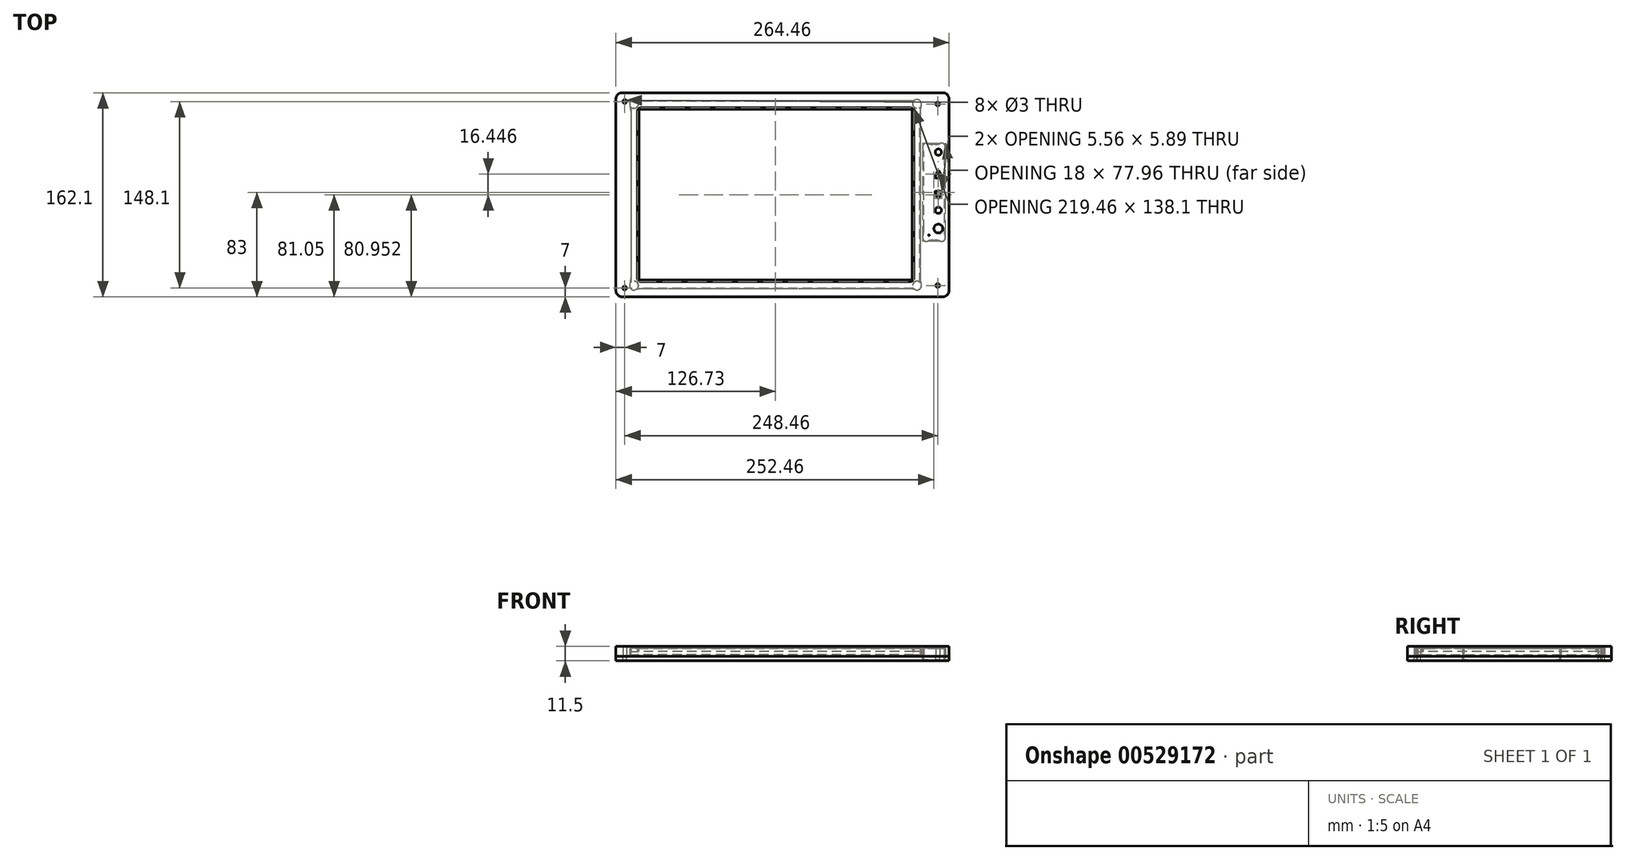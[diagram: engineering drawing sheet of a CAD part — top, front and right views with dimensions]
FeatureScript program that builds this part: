
annotation { "Feature Type Name" : "Feature", "Feature Type Description" : "" }
export const myFeature = defineFeature(function(context is Context, id is Id, definition is map)
    precondition{}
    {
        {
            var Q0;
            Q0=qCreatedBy(makeId("Top.planeOp"),FACE);
            var sketch = newSketch(context, id + "F0", { "sketchPlane" : qUnion([Q0])});
            skLineSegment(sketch, "E0.bottom", {"start": v(-121.73, 81.05) * mm, "end": v(132.73, 81.05) * mm});
            skLineSegment(sketch, "E0.top", {"start": v(-121.73, -81.05) * mm, "end": v(132.73, -81.05) * mm});
            skLineSegment(sketch, "E0.left", {"start": v(-126.73, 76.05) * mm, "end": v(-126.73, -76.05) * mm});
            skLineSegment(sketch, "E0.right", {"start": v(137.73, 76.05) * mm, "end": v(137.73, -76.05) * mm});
            skLineSegment(sketch, "E1.bottom", {"start": v(-106.73, 69.05) * mm, "end": v(106.73, 69.05) * mm});
            skLineSegment(sketch, "E1.top", {"start": v(-106.73, -69.05) * mm, "end": v(106.73, -69.05) * mm});
            skLineSegment(sketch, "E1.left", {"start": v(-109.73, 66.05) * mm, "end": v(-109.73, -66.05) * mm});
            skLineSegment(sketch, "E1.right", {"start": v(109.73, 66.05) * mm, "end": v(109.73, -66.05) * mm});
            skPoint(sketch, "E2.visualSharp", {"position": v(-126.73, 81.05) * mm});
            skArc(sketch, "E2.filletArc", {"start": v(-121.73, 81.05) * mm, "mid": v(-125.27, 79.59) * mm, "end": v(-126.73, 76.05) * mm});
            skPoint(sketch, "E3.visualSharp", {"position": v(-126.73, -81.05) * mm});
            skArc(sketch, "E3.filletArc", {"start": v(-126.73, -76.05) * mm, "mid": v(-125.27, -79.59) * mm, "end": v(-121.73, -81.05) * mm});
            skPoint(sketch, "E4.visualSharp", {"position": v(137.73, -81.05) * mm});
            skArc(sketch, "E4.filletArc", {"start": v(132.73, -81.05) * mm, "mid": v(136.27, -79.59) * mm, "end": v(137.73, -76.05) * mm});
            skPoint(sketch, "E5.visualSharp", {"position": v(137.73, 81.05) * mm});
            skArc(sketch, "E5.filletArc", {"start": v(137.73, 76.05) * mm, "mid": v(136.27, 79.59) * mm, "end": v(132.73, 81.05) * mm});
            skCircle(sketch, "E6", {"center": v(129.23, 33.85) * mm, "radius": 2.5 * mm});
            skLineSegment(sketch, "E7", {"start": v(129.23, 33.85) * mm, "end": v(129.23, -36.05) * mm, "construction": true});
            skCircle(sketch, "E8", {"center": v(129.23, -12.32) * mm, "radius": 2.5 * mm});
            skPoint(sketch, "E9", {"position": v(129.23, -1.1) * mm});
            skCircle(sketch, "E10", {"center": v(129.23, -26.87) * mm, "radius": 3.5 * mm});
            skCircle(sketch, "E11", {"center": v(129.23, 15.98) * mm, "radius": 4 * mm, "construction": true});
            skLineSegment(sketch, "E12", {"start": v(128.78, 19) * mm, "end": v(126.5, 14.12) * mm});
            skLineSegment(sketch, "E13", {"start": v(126.95, 13.4) * mm, "end": v(131.5, 13.4) * mm});
            skLineSegment(sketch, "E14", {"start": v(131.96, 14.12) * mm, "end": v(129.68, 19) * mm});
            skCircle(sketch, "E15", {"center": v(129.23, 0.28) * mm, "radius": 4 * mm, "construction": true});
            skLineSegment(sketch, "E16", {"start": v(129.68, -2.75) * mm, "end": v(131.96, 2.13) * mm});
            skLineSegment(sketch, "E17", {"start": v(131.5, 2.85) * mm, "end": v(126.95, 2.85) * mm});
            skLineSegment(sketch, "E18", {"start": v(126.5, 2.13) * mm, "end": v(128.78, -2.75) * mm});
            skLineSegment(sketch, "E19.bottom", {"start": v(117.73, 39.95) * mm, "end": v(133.73, 39.95) * mm, "construction": true});
            skLineSegment(sketch, "E19.top", {"start": v(117.73, -36.05) * mm, "end": v(133.73, -36.05) * mm, "construction": true});
            skLineSegment(sketch, "E19.left", {"start": v(117.73, 39.95) * mm, "end": v(117.73, -36.05) * mm, "construction": true});
            skLineSegment(sketch, "E19.right", {"start": v(133.73, 39.95) * mm, "end": v(133.73, -36.05) * mm, "construction": true});
            skPoint(sketch, "E20.visualSharp", {"position": v(129.23, 19.98) * mm});
            skArc(sketch, "E20.filletArc", {"start": v(129.68, 19) * mm, "mid": v(129.23, 19.3) * mm, "end": v(128.78, 19) * mm});
            skPoint(sketch, "E21.visualSharp", {"position": v(126.17, 13.4) * mm});
            skArc(sketch, "E21.filletArc", {"start": v(126.5, 14.12) * mm, "mid": v(126.53, 13.64) * mm, "end": v(126.95, 13.4) * mm});
            skPoint(sketch, "E22.visualSharp", {"position": v(132.3, 13.4) * mm});
            skArc(sketch, "E22.filletArc", {"start": v(131.5, 13.4) * mm, "mid": v(131.93, 13.64) * mm, "end": v(131.96, 14.12) * mm});
            skPoint(sketch, "E23.visualSharp", {"position": v(126.17, 2.85) * mm});
            skArc(sketch, "E23.filletArc", {"start": v(126.95, 2.85) * mm, "mid": v(126.53, 2.61) * mm, "end": v(126.5, 2.13) * mm});
            skPoint(sketch, "E24.visualSharp", {"position": v(132.3, 2.85) * mm});
            skArc(sketch, "E24.filletArc", {"start": v(131.96, 2.13) * mm, "mid": v(131.93, 2.61) * mm, "end": v(131.5, 2.85) * mm});
            skPoint(sketch, "E25.visualSharp", {"position": v(129.23, -3.72) * mm});
            skArc(sketch, "E25.filletArc", {"start": v(128.78, -2.75) * mm, "mid": v(129.23, -3.04) * mm, "end": v(129.68, -2.75) * mm});
            skCircle(sketch, "E26", {"center": v(121.73, -32.05) * mm, "radius": 0.35 * mm});
            skCircle(sketch, "E27", {"center": v(128.73, 72.05) * mm, "radius": 1.5 * mm});
            skCircle(sketch, "E28", {"center": v(-119.73, 74.05) * mm, "radius": 1.5 * mm});
            skCircle(sketch, "E29.MirrorC", {"center": v(128.73, -72.05) * mm, "radius": 1.5 * mm});
            skCircle(sketch, "E30.MirrorC", {"center": v(-119.73, -74.05) * mm, "radius": 1.5 * mm});
            skPoint(sketch, "E31.visualSharp", {"position": v(-109.73, 69.05) * mm});
            skArc(sketch, "E31.filletArc", {"start": v(-106.73, 69.05) * mm, "mid": v(-108.85, 68.17) * mm, "end": v(-109.73, 66.05) * mm});
            skPoint(sketch, "E32.visualSharp", {"position": v(-109.73, -69.05) * mm});
            skArc(sketch, "E32.filletArc", {"start": v(-109.73, -66.05) * mm, "mid": v(-108.85, -68.17) * mm, "end": v(-106.73, -69.05) * mm});
            skPoint(sketch, "E33.visualSharp", {"position": v(109.73, -69.05) * mm});
            skArc(sketch, "E33.filletArc", {"start": v(106.73, -69.05) * mm, "mid": v(108.85, -68.17) * mm, "end": v(109.73, -66.05) * mm});
            skPoint(sketch, "E34.visualSharp", {"position": v(109.73, 69.05) * mm});
            skArc(sketch, "E34.filletArc", {"start": v(109.73, 66.05) * mm, "mid": v(108.85, 68.17) * mm, "end": v(106.73, 69.05) * mm});
            skSolve(sketch);
        }
        {
            var Q0;
            Q0=makeQuery(id+"F0.imprint","IMPRINT",FACE,{"disambiguationData":[TD([[makeQuery(id+"F0.imprint","IMPRINT",EDGE,{"derivedFrom":sQuery(id+"F0.wireOp",EDGE,"E0.bottom")}),-1.0]])]});
            extrude(context, id + "F1", {"entities" : qUnion([Q0]), "depth" : 8 * mm, "offsetDistance" : 25 * mm});
        }
        {
            var Q0;
            Q0=makeQuery(id+"F1.opExtrude","CAP_FACE",FACE,{"disambiguationData":[OSD([sQuery(id+"F0.wireOp",EDGE,"E0.bottom"),sQuery(id+"F0.wireOp",EDGE,"E0.top"),sQuery(id+"F0.wireOp",EDGE,"E0.left"),sQuery(id+"F0.wireOp",EDGE,"E0.right"),sQuery(id+"F0.wireOp",EDGE,"E1.bottom"),sQuery(id+"F0.wireOp",EDGE,"E1.top"),sQuery(id+"F0.wireOp",EDGE,"E1.left"),sQuery(id+"F0.wireOp",EDGE,"E1.right"),sQuery(id+"F0.wireOp",EDGE,"E2.filletArc"),sQuery(id+"F0.wireOp",EDGE,"E3.filletArc"),sQuery(id+"F0.wireOp",EDGE,"E4.filletArc"),sQuery(id+"F0.wireOp",EDGE,"E5.filletArc"),sQuery(id+"F0.wireOp",EDGE,"E6"),sQuery(id+"F0.wireOp",EDGE,"E8"),sQuery(id+"F0.wireOp",EDGE,"E10"),sQuery(id+"F0.wireOp",EDGE,"E12"),sQuery(id+"F0.wireOp",EDGE,"E13"),sQuery(id+"F0.wireOp",EDGE,"E14"),sQuery(id+"F0.wireOp",EDGE,"E16"),sQuery(id+"F0.wireOp",EDGE,"E17"),sQuery(id+"F0.wireOp",EDGE,"E18"),sQuery(id+"F0.wireOp",EDGE,"E20.filletArc"),sQuery(id+"F0.wireOp",EDGE,"E21.filletArc"),sQuery(id+"F0.wireOp",EDGE,"E22.filletArc"),sQuery(id+"F0.wireOp",EDGE,"E23.filletArc"),sQuery(id+"F0.wireOp",EDGE,"E24.filletArc"),sQuery(id+"F0.wireOp",EDGE,"E25.filletArc"),sQuery(id+"F0.wireOp",EDGE,"E26"),sQuery(id+"F0.wireOp",EDGE,"E27"),sQuery(id+"F0.wireOp",EDGE,"E28"),sQuery(id+"F0.wireOp",EDGE,"E29.MirrorC"),sQuery(id+"F0.wireOp",EDGE,"E30.MirrorC")])],"isStart":true});
            var sketch = newSketch(context, id + "F2", { "sketchPlane" : qUnion([Q0])});
            skLineSegment(sketch, "E35.bottom", {"start": v(114.8, -74.6) * mm, "end": v(-114.8, -74.6) * mm});
            skLineSegment(sketch, "E35.top", {"start": v(114.8, 74.6) * mm, "end": v(-114.8, 74.6) * mm});
            skLineSegment(sketch, "E35.left", {"start": v(114.8, -74.6) * mm, "end": v(114.8, 74.6) * mm});
            skLineSegment(sketch, "E35.right", {"start": v(-114.8, -74.6) * mm, "end": v(-114.8, 74.6) * mm});
            skSolve(sketch);
        }
        {
            var Q0;
            Q0 = qSketchRegion(id + "F2", true);
            extrude(context, id + "F3", {"entities" : qUnion([Q0]), "operationType" : NewBodyOperationType.REMOVE, "oppositeDirection" : true, "depth" : 6.5 * mm, "offsetDistance" : 25 * mm});
        }
        {
            var Q0;
            Q0 = qSketchRegion(id + "F2", true);
            extrude(context, id + "F4", {"entities" : qUnion([Q0]), "oppositeDirection" : true, "depth" : 6.5 * mm, "offsetDistance" : 25 * mm, "hasSecondDirection" : true, "secondDirectionOppositeDirection" : true, "secondDirectionDepth" : 4 * mm});
        }
        {
            var Q0;
            Q0=makeQuery(id+"F4.opExtrude","CAP_FACE",FACE,{"disambiguationData":[OSD([sQuery(id+"F2.wireOp",EDGE,"E35.bottom"),sQuery(id+"F2.wireOp",EDGE,"E35.top"),sQuery(id+"F2.wireOp",EDGE,"E35.left"),sQuery(id+"F2.wireOp",EDGE,"E35.right")])],"isStart":false});
            var sketch = newSketch(context, id + "F5", { "sketchPlane" : qUnion([Q0])});
            skLineSegment(sketch, "E36.bottom", {"start": v(-108.48, 67.8) * mm, "end": v(108.48, 67.8) * mm});
            skLineSegment(sketch, "E36.top", {"start": v(-108.48, -67.8) * mm, "end": v(108.48, -67.8) * mm});
            skLineSegment(sketch, "E36.left", {"start": v(-108.48, 67.8) * mm, "end": v(-108.48, -67.8) * mm});
            skLineSegment(sketch, "E36.right", {"start": v(108.48, 67.8) * mm, "end": v(108.48, -67.8) * mm});
            skSolve(sketch);
        }
        {
            var Q0;
            Q0 = qSketchRegion(id + "F5", true);
            extrude(context, id + "F6", {"entities" : qUnion([Q0]), "operationType" : NewBodyOperationType.ADD, "depth" : 0.5 * mm, "offsetDistance" : 25 * mm});
        }
        {
            var Q0;
            Q0=makeQuery(id+"F0.imprint","IMPRINT",FACE,{"disambiguationData":[TD([[makeQuery(id+"F0.imprint","IMPRINT",EDGE,{"derivedFrom":sQuery(id+"F0.wireOp",EDGE,"E0.bottom")}),-1.0]])]});
            var sketch = newSketch(context, id + "F7", { "sketchPlane" : qUnion([Q0])});
            skLineSegment(sketch, "E37.bottom", {"start": v(131.73, 40.95) * mm, "end": v(119.73, 40.95) * mm, "construction": true});
            skLineSegment(sketch, "E37.top", {"start": v(131.73, -37.05) * mm, "end": v(119.73, -37.05) * mm, "construction": true});
            skLineSegment(sketch, "E37.left", {"start": v(134.73, 37.95) * mm, "end": v(134.73, -34.05) * mm, "construction": true});
            skLineSegment(sketch, "E37.right", {"start": v(116.73, 37.95) * mm, "end": v(116.73, -34.05) * mm, "construction": true});
            skPoint(sketch, "E38.visualSharp", {"position": v(134.73, 40.95) * mm});
            skArc(sketch, "E38.filletArc", {"start": v(134.73, 37.95) * mm, "mid": v(133.85, 40.07) * mm, "end": v(131.73, 40.95) * mm});
            skPoint(sketch, "E39.visualSharp", {"position": v(116.73, 40.95) * mm});
            skArc(sketch, "E39.filletArc", {"start": v(119.73, 40.95) * mm, "mid": v(117.6, 40.07) * mm, "end": v(116.73, 37.95) * mm});
            skPoint(sketch, "E40.visualSharp", {"position": v(116.73, -37.05) * mm});
            skArc(sketch, "E40.filletArc", {"start": v(116.73, -34.05) * mm, "mid": v(117.6, -36.17) * mm, "end": v(119.73, -37.05) * mm});
            skPoint(sketch, "E41.visualSharp", {"position": v(134.73, -37.05) * mm});
            skArc(sketch, "E41.filletArc", {"start": v(131.73, -37.05) * mm, "mid": v(133.85, -36.17) * mm, "end": v(134.73, -34.05) * mm});
            skArc(sketch, "E42", {"start": v(119.73, -37.05) * mm, "mid": v(120.32, -37) * mm, "end": v(120.88, -36.82) * mm});
            skArc(sketch, "E43", {"start": v(130.58, -36.82) * mm, "mid": v(131.14, -37) * mm, "end": v(131.73, -37.05) * mm});
            skLineSegment(sketch, "E44", {"start": v(124.73, -36.05) * mm, "end": v(126.73, -36.05) * mm});
            skArc(sketch, "E45", {"start": v(116.73, -34.05) * mm, "mid": v(116.76, -33.6) * mm, "end": v(116.86, -33.18) * mm});
            skArc(sketch, "E46", {"start": v(116.73, 37.95) * mm, "mid": v(116.76, 37.5) * mm, "end": v(116.86, 37.08) * mm});
            skLineSegment(sketch, "E47", {"start": v(117.73, -27.34) * mm, "end": v(117.73, 31.24) * mm});
            skPoint(sketch, "E48.orphan", {"position": v(119.73, 34.95) * mm});
            skArc(sketch, "E49", {"start": v(119.73, 40.95) * mm, "mid": v(120.32, 40.9) * mm, "end": v(120.88, 40.72) * mm});
            skArc(sketch, "E50", {"start": v(131.73, 40.95) * mm, "mid": v(131.14, 40.9) * mm, "end": v(130.58, 40.72) * mm});
            skLineSegment(sketch, "E51", {"start": v(126.73, 39.95) * mm, "end": v(124.73, 39.95) * mm});
            skArc(sketch, "E52", {"start": v(134.73, 37.95) * mm, "mid": v(134.7, 37.5) * mm, "end": v(134.6, 37.08) * mm});
            skArc(sketch, "E53", {"start": v(134.73, -34.05) * mm, "mid": v(134.7, -33.6) * mm, "end": v(134.6, -33.18) * mm});
            skLineSegment(sketch, "E54", {"start": v(133.73, 31.24) * mm, "end": v(133.73, -27.34) * mm});
            skPoint(sketch, "E55.visualSharp", {"position": v(133.73, 35.71) * mm});
            skArc(sketch, "E55.filletArc", {"start": v(134.6, 37.08) * mm, "mid": v(133.95, 34.2) * mm, "end": v(133.73, 31.24) * mm});
            skPoint(sketch, "E56.visualSharp", {"position": v(133.73, -31.81) * mm});
            skArc(sketch, "E56.filletArc", {"start": v(133.73, -27.34) * mm, "mid": v(133.95, -30.3) * mm, "end": v(134.6, -33.18) * mm});
            skPoint(sketch, "E57.visualSharp", {"position": v(117.73, -31.81) * mm});
            skArc(sketch, "E57.filletArc", {"start": v(116.86, -33.18) * mm, "mid": v(117.51, -30.3) * mm, "end": v(117.73, -27.34) * mm});
            skPoint(sketch, "E58.visualSharp", {"position": v(117.73, 35.71) * mm});
            skArc(sketch, "E58.filletArc", {"start": v(117.73, 31.24) * mm, "mid": v(117.51, 34.2) * mm, "end": v(116.86, 37.08) * mm});
            skPoint(sketch, "E59.visualSharp", {"position": v(121.97, 39.95) * mm});
            skArc(sketch, "E59.filletArc", {"start": v(120.88, 40.72) * mm, "mid": v(122.77, 40.14) * mm, "end": v(124.73, 39.95) * mm});
            skPoint(sketch, "E60.visualSharp", {"position": v(129.5, 39.95) * mm});
            skArc(sketch, "E60.filletArc", {"start": v(126.73, 39.95) * mm, "mid": v(128.7, 40.14) * mm, "end": v(130.58, 40.72) * mm});
            skPoint(sketch, "E61.visualSharp", {"position": v(121.97, -36.05) * mm});
            skArc(sketch, "E61.filletArc", {"start": v(124.73, -36.05) * mm, "mid": v(122.77, -36.24) * mm, "end": v(120.88, -36.82) * mm});
            skPoint(sketch, "E62.visualSharp", {"position": v(129.5, -36.05) * mm});
            skArc(sketch, "E62.filletArc", {"start": v(130.58, -36.82) * mm, "mid": v(128.7, -36.24) * mm, "end": v(126.73, -36.05) * mm});
            skSolve(sketch);
        }
        {
            var Q0;
            Q0 = qSketchRegion(id + "F7", true);
            extrude(context, id + "F8", {"entities" : qUnion([Q0]), "operationType" : NewBodyOperationType.REMOVE, "depth" : 6.5 * mm, "offsetDistance" : 25 * mm});
        }
        {
            var Q0;
            Q0=qCreatedBy(makeId("Top.planeOp"),FACE);
            var sketch = newSketch(context, id + "F9", { "sketchPlane" : qUnion([Q0])});
            skLineSegment(sketch, "E63.0", {"start": v(132.73, -81.05) * mm, "end": v(-121.73, -81.05) * mm});
            skArc(sketch, "E63.1", {"start": v(137.73, -76.05) * mm, "mid": v(136.27, -79.59) * mm, "end": v(132.73, -81.05) * mm});
            skArc(sketch, "E63.2", {"start": v(-121.73, -81.05) * mm, "mid": v(-125.27, -79.59) * mm, "end": v(-126.73, -76.05) * mm});
            skLineSegment(sketch, "E63.3", {"start": v(137.73, 76.05) * mm, "end": v(137.73, -76.05) * mm});
            skLineSegment(sketch, "E63.4", {"start": v(-126.73, -76.05) * mm, "end": v(-126.73, 76.05) * mm});
            skArc(sketch, "E63.5", {"start": v(-126.73, 76.05) * mm, "mid": v(-125.27, 79.59) * mm, "end": v(-121.73, 81.05) * mm});
            skLineSegment(sketch, "E63.6", {"start": v(-121.73, 81.05) * mm, "end": v(132.73, 81.05) * mm});
            skArc(sketch, "E63.7", {"start": v(132.73, 81.05) * mm, "mid": v(136.27, 79.59) * mm, "end": v(137.73, 76.05) * mm});
            skCircle(sketch, "E64.0", {"center": v(128.73, 72.05) * mm, "radius": 1.5 * mm});
            skCircle(sketch, "E65.0", {"center": v(128.73, -72.05) * mm, "radius": 1.5 * mm});
            skCircle(sketch, "E66.0", {"center": v(-119.73, -74.05) * mm, "radius": 1.5 * mm});
            skCircle(sketch, "E67.0", {"center": v(-119.73, 74.05) * mm, "radius": 1.5 * mm});
            skSolve(sketch);
        }
        {
            var Q0;
            Q0 = qSketchRegion(id + "F9", true);
            extrude(context, id + "F10", {"entities" : qUnion([Q0]), "oppositeDirection" : true, "depth" : 3.5 * mm, "offsetDistance" : 25 * mm});
        }
        {
            var Q0;
            Q0 = qSketchRegion(id + "F7", true);
            extrude(context, id + "F11", {"entities" : qUnion([Q0]), "operationType" : NewBodyOperationType.REMOVE, "oppositeDirection" : true, "depth" : 2.7 * mm, "offsetDistance" : 25 * mm});
        }
        {
            var Q0;
            Q0=makeQuery(id+"F10.opExtrude","CAP_FACE",FACE,{"disambiguationData":[OSD([sQuery(id+"F9.wireOp",EDGE,"E63.0"),sQuery(id+"F9.wireOp",EDGE,"E63.1"),sQuery(id+"F9.wireOp",EDGE,"E63.2"),sQuery(id+"F9.wireOp",EDGE,"E63.3"),sQuery(id+"F9.wireOp",EDGE,"E63.4"),sQuery(id+"F9.wireOp",EDGE,"E63.5"),sQuery(id+"F9.wireOp",EDGE,"E63.6"),sQuery(id+"F9.wireOp",EDGE,"E63.7")])],"isStart":true});
            var sketch = newSketch(context, id + "F12", { "sketchPlane" : qUnion([Q0])});
            skLineSegment(sketch, "E68.bottom", {"start": v(113.58, -74.25) * mm, "end": v(-113.58, -74.25) * mm});
            skLineSegment(sketch, "E68.top", {"start": v(113.58, 74.25) * mm, "end": v(-113.58, 74.25) * mm});
            skLineSegment(sketch, "E68.left", {"start": v(114.58, -73.25) * mm, "end": v(114.58, 73.25) * mm});
            skLineSegment(sketch, "E68.right", {"start": v(-114.58, -73.25) * mm, "end": v(-114.58, 73.25) * mm});
            skPoint(sketch, "E69.visualSharp", {"position": v(114.58, -74.25) * mm});
            skArc(sketch, "E69.filletArc", {"start": v(113.58, -74.25) * mm, "mid": v(114.29, -73.96) * mm, "end": v(114.58, -73.25) * mm});
            skPoint(sketch, "E70.visualSharp", {"position": v(-114.58, -74.25) * mm});
            skArc(sketch, "E70.filletArc", {"start": v(-114.58, -73.25) * mm, "mid": v(-114.29, -73.96) * mm, "end": v(-113.58, -74.25) * mm});
            skPoint(sketch, "E71.visualSharp", {"position": v(-114.58, 74.25) * mm});
            skArc(sketch, "E71.filletArc", {"start": v(-113.58, 74.25) * mm, "mid": v(-114.29, 73.96) * mm, "end": v(-114.58, 73.25) * mm});
            skPoint(sketch, "E72.visualSharp", {"position": v(114.58, 74.25) * mm});
            skArc(sketch, "E72.filletArc", {"start": v(114.58, 73.25) * mm, "mid": v(114.29, 73.96) * mm, "end": v(113.58, 74.25) * mm});
            skSolve(sketch);
        }
        {
            var Q0;
            Q0 = qSketchRegion(id + "F12", true);
            extrude(context, id + "F13", {"entities" : qUnion([Q0]), "operationType" : NewBodyOperationType.ADD, "depth" : 1.5 * mm, "offsetDistance" : 25 * mm});
        }
        {
            var Q0;
            Q0=makeQuery(id+"F1.opExtrude","CAP_FACE",FACE,{"disambiguationData":[OSD([sQuery(id+"F0.wireOp",EDGE,"E0.bottom"),sQuery(id+"F0.wireOp",EDGE,"E0.top"),sQuery(id+"F0.wireOp",EDGE,"E0.left"),sQuery(id+"F0.wireOp",EDGE,"E0.right"),sQuery(id+"F0.wireOp",EDGE,"E1.bottom"),sQuery(id+"F0.wireOp",EDGE,"E1.top"),sQuery(id+"F0.wireOp",EDGE,"E1.left"),sQuery(id+"F0.wireOp",EDGE,"E1.right"),sQuery(id+"F0.wireOp",EDGE,"E2.filletArc"),sQuery(id+"F0.wireOp",EDGE,"E3.filletArc"),sQuery(id+"F0.wireOp",EDGE,"E4.filletArc"),sQuery(id+"F0.wireOp",EDGE,"E5.filletArc"),sQuery(id+"F0.wireOp",EDGE,"E6"),sQuery(id+"F0.wireOp",EDGE,"E8"),sQuery(id+"F0.wireOp",EDGE,"E10"),sQuery(id+"F0.wireOp",EDGE,"E12"),sQuery(id+"F0.wireOp",EDGE,"E13"),sQuery(id+"F0.wireOp",EDGE,"E14"),sQuery(id+"F0.wireOp",EDGE,"E16"),sQuery(id+"F0.wireOp",EDGE,"E17"),sQuery(id+"F0.wireOp",EDGE,"E18"),sQuery(id+"F0.wireOp",EDGE,"E20.filletArc"),sQuery(id+"F0.wireOp",EDGE,"E21.filletArc"),sQuery(id+"F0.wireOp",EDGE,"E22.filletArc"),sQuery(id+"F0.wireOp",EDGE,"E23.filletArc"),sQuery(id+"F0.wireOp",EDGE,"E24.filletArc"),sQuery(id+"F0.wireOp",EDGE,"E25.filletArc"),sQuery(id+"F0.wireOp",EDGE,"E26"),sQuery(id+"F0.wireOp",EDGE,"E27"),sQuery(id+"F0.wireOp",EDGE,"E28"),sQuery(id+"F0.wireOp",EDGE,"E29.MirrorC"),sQuery(id+"F0.wireOp",EDGE,"E30.MirrorC"),sQuery(id+"F0.wireOp",EDGE,"E31.filletArc"),sQuery(id+"F0.wireOp",EDGE,"E32.filletArc"),sQuery(id+"F0.wireOp",EDGE,"E33.filletArc"),sQuery(id+"F0.wireOp",EDGE,"E34.filletArc")])],"isStart":true});
            var sketch = newSketch(context, id + "F14", { "sketchPlane" : qUnion([Q0])});
            skCircle(sketch, "E73", {"center": v(-112.3, -72.15) * mm, "radius": 3.5 * mm});
            skCircle(sketch, "E74", {"center": v(-112.3, 72.15) * mm, "radius": 3.5 * mm});
            skCircle(sketch, "E75", {"center": v(112.3, 72.15) * mm, "radius": 3.5 * mm});
            skCircle(sketch, "E76", {"center": v(112.3, -72.15) * mm, "radius": 3.5 * mm});
            skSolve(sketch);
        }
        {
            var Q0;
            Q0 = qSketchRegion(id + "F14", true);
            extrude(context, id + "F15", {"entities" : qUnion([Q0]), "operationType" : NewBodyOperationType.REMOVE, "oppositeDirection" : true, "depth" : 6.5 * mm, "offsetDistance" : 25 * mm});
        }
        {
            var Q0;
            Q0=makeQuery(id+"F15.boolean.opBoolean","INTERSECT",EDGE,{"derivedFrom":[makeQuery(id+"F3.boolean.opBoolean","COPY",FACE,{"derivedFrom":makeQuery(id+"F3.opExtrude","SWEPT_FACE",FACE,{"disambiguationData":[OSD([sQuery(id+"F2.wireOp",EDGE,"E35.left")])]})}),makeQuery(id+"F15.opExtrude","SWEPT_FACE",FACE,{"disambiguationData":[OSD([sQuery(id+"F14.wireOp",EDGE,"E76")])]})]});
            var Q1;
            Q1=makeQuery(id+"F15.boolean.opBoolean","INTERSECT",EDGE,{"derivedFrom":[makeQuery(id+"F3.boolean.opBoolean","COPY",FACE,{"derivedFrom":makeQuery(id+"F3.opExtrude","SWEPT_FACE",FACE,{"disambiguationData":[OSD([sQuery(id+"F2.wireOp",EDGE,"E35.bottom")])]})}),makeQuery(id+"F15.opExtrude","SWEPT_FACE",FACE,{"disambiguationData":[OSD([sQuery(id+"F14.wireOp",EDGE,"E76")])]})]});
            var Q2;
            Q2=makeQuery(id+"F15.boolean.opBoolean","INTERSECT",EDGE,{"derivedFrom":[makeQuery(id+"F3.boolean.opBoolean","COPY",FACE,{"derivedFrom":makeQuery(id+"F3.opExtrude","SWEPT_FACE",FACE,{"disambiguationData":[OSD([sQuery(id+"F2.wireOp",EDGE,"E35.left")])]})}),makeQuery(id+"F15.opExtrude","SWEPT_FACE",FACE,{"disambiguationData":[OSD([sQuery(id+"F14.wireOp",EDGE,"E75")])]})]});
            var Q3;
            Q3=makeQuery(id+"F15.boolean.opBoolean","INTERSECT",EDGE,{"derivedFrom":[makeQuery(id+"F3.boolean.opBoolean","COPY",FACE,{"derivedFrom":makeQuery(id+"F3.opExtrude","SWEPT_FACE",FACE,{"disambiguationData":[OSD([sQuery(id+"F2.wireOp",EDGE,"E35.top")])]})}),makeQuery(id+"F15.opExtrude","SWEPT_FACE",FACE,{"disambiguationData":[OSD([sQuery(id+"F14.wireOp",EDGE,"E75")])]})]});
            var Q4;
            Q4=makeQuery(id+"F15.boolean.opBoolean","INTERSECT",EDGE,{"derivedFrom":[makeQuery(id+"F3.boolean.opBoolean","COPY",FACE,{"derivedFrom":makeQuery(id+"F3.opExtrude","SWEPT_FACE",FACE,{"disambiguationData":[OSD([sQuery(id+"F2.wireOp",EDGE,"E35.top")])]})}),makeQuery(id+"F15.opExtrude","SWEPT_FACE",FACE,{"disambiguationData":[OSD([sQuery(id+"F14.wireOp",EDGE,"E74")])]})]});
            var Q5;
            Q5=makeQuery(id+"F15.boolean.opBoolean","INTERSECT",EDGE,{"derivedFrom":[makeQuery(id+"F3.boolean.opBoolean","COPY",FACE,{"derivedFrom":makeQuery(id+"F3.opExtrude","SWEPT_FACE",FACE,{"disambiguationData":[OSD([sQuery(id+"F2.wireOp",EDGE,"E35.right")])]})}),makeQuery(id+"F15.opExtrude","SWEPT_FACE",FACE,{"disambiguationData":[OSD([sQuery(id+"F14.wireOp",EDGE,"E74")])]})]});
            var Q6;
            Q6=makeQuery(id+"F15.boolean.opBoolean","INTERSECT",EDGE,{"derivedFrom":[makeQuery(id+"F3.boolean.opBoolean","COPY",FACE,{"derivedFrom":makeQuery(id+"F3.opExtrude","SWEPT_FACE",FACE,{"disambiguationData":[OSD([sQuery(id+"F2.wireOp",EDGE,"E35.right")])]})}),makeQuery(id+"F15.opExtrude","SWEPT_FACE",FACE,{"disambiguationData":[OSD([sQuery(id+"F14.wireOp",EDGE,"E73")])]})]});
            var Q7;
            Q7=makeQuery(id+"F15.boolean.opBoolean","INTERSECT",EDGE,{"derivedFrom":[makeQuery(id+"F3.boolean.opBoolean","COPY",FACE,{"derivedFrom":makeQuery(id+"F3.opExtrude","SWEPT_FACE",FACE,{"disambiguationData":[OSD([sQuery(id+"F2.wireOp",EDGE,"E35.bottom")])]})}),makeQuery(id+"F15.opExtrude","SWEPT_FACE",FACE,{"disambiguationData":[OSD([sQuery(id+"F14.wireOp",EDGE,"E73")])]})]});
            fillet(context, id + "F16", {"entities" : qUnion([Q0, Q1, Q2, Q3, Q4, Q5, Q6, Q7]), "radius" : 15 * mm, "tangentPropagation" : true, "allowEdgeOverflow" : false});
        }
    });
